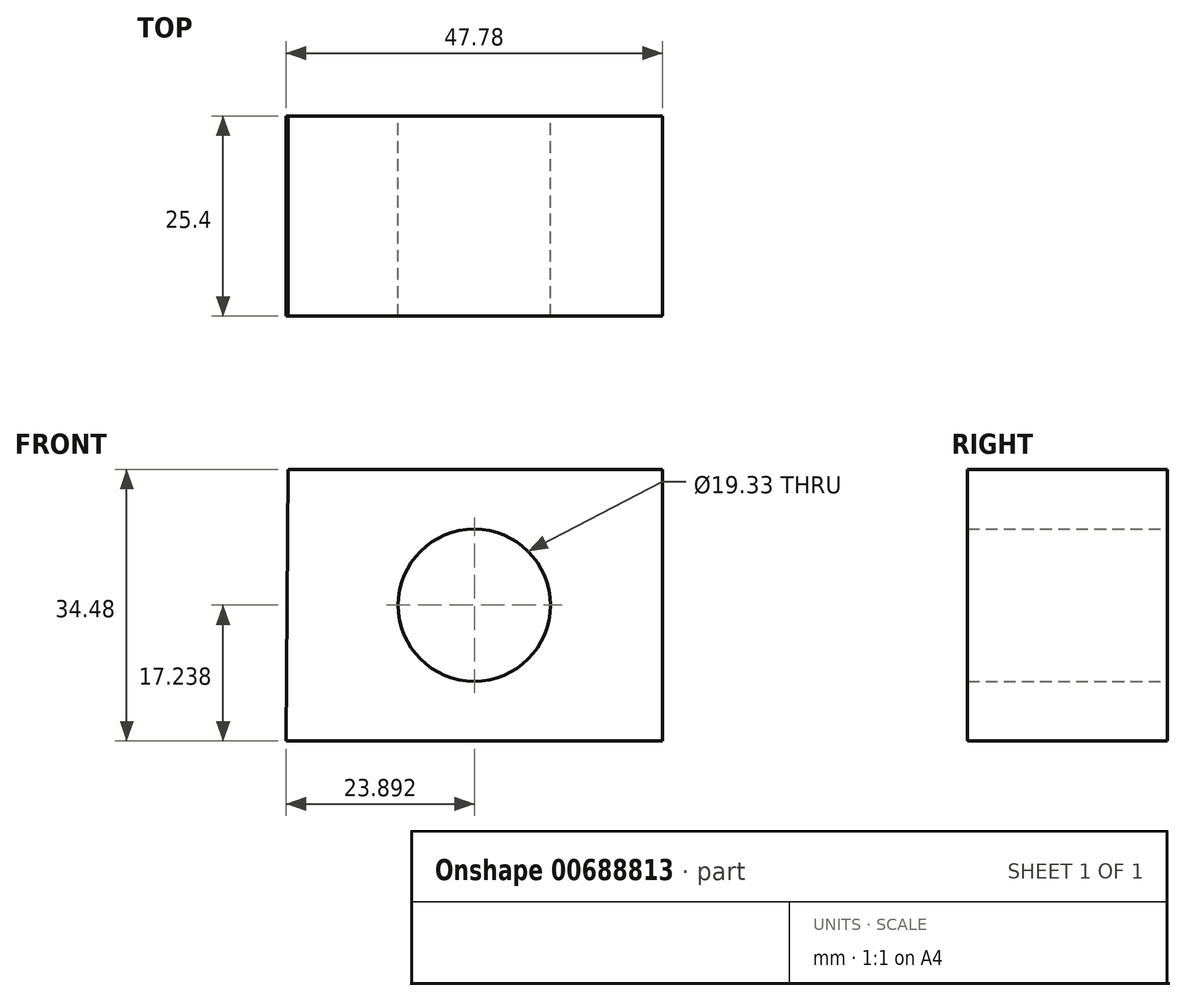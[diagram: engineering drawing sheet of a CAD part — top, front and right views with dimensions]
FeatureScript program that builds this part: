
annotation { "Feature Type Name" : "Feature", "Feature Type Description" : "" }
export const myFeature = defineFeature(function(context is Context, id is Id, definition is map)
    precondition{}
    {
        {
            var Q0;
            Q0=qCreatedBy(makeId("Front.planeOp"),FACE);
            var sketch = newSketch(context, id + "F0", { "sketchPlane" : qUnion([Q0])});
            skLineSegment(sketch, "E0", {"start": v(-18.76, 31.6) * mm, "end": v(28.8, 31.6) * mm});
            skLineSegment(sketch, "E1", {"start": v(28.8, 31.6) * mm, "end": v(28.8, -2.87) * mm});
            skLineSegment(sketch, "E2", {"start": v(28.8, -2.87) * mm, "end": v(-18.99, -2.87) * mm});
            skLineSegment(sketch, "E3", {"start": v(-18.99, -2.87) * mm, "end": v(-18.76, 31.6) * mm});
            skCircle(sketch, "E4", {"center": v(4.9, 14.37) * mm, "radius": 9.67 * mm});
            skPoint(sketch, "E5", {"position": v(-18.88, 14.37) * mm});
            skPoint(sketch, "E6", {"position": v(4.9, -2.87) * mm});
            skSolve(sketch);
        }
        {
            var Q0;
            Q0=makeQuery(id+"F0.imprint","IMPRINT",FACE,{"disambiguationData":[TD([[makeQuery(id+"F0.imprint","IMPRINT",EDGE,{"derivedFrom":sQuery(id+"F0.wireOp",EDGE,"E0")}),-1.0]])]});
            extrude(context, id + "F1", {"entities" : qUnion([Q0]), "depth" : 25.4 * mm, "offsetDistance" : 25.4 * mm});
        }
    });
